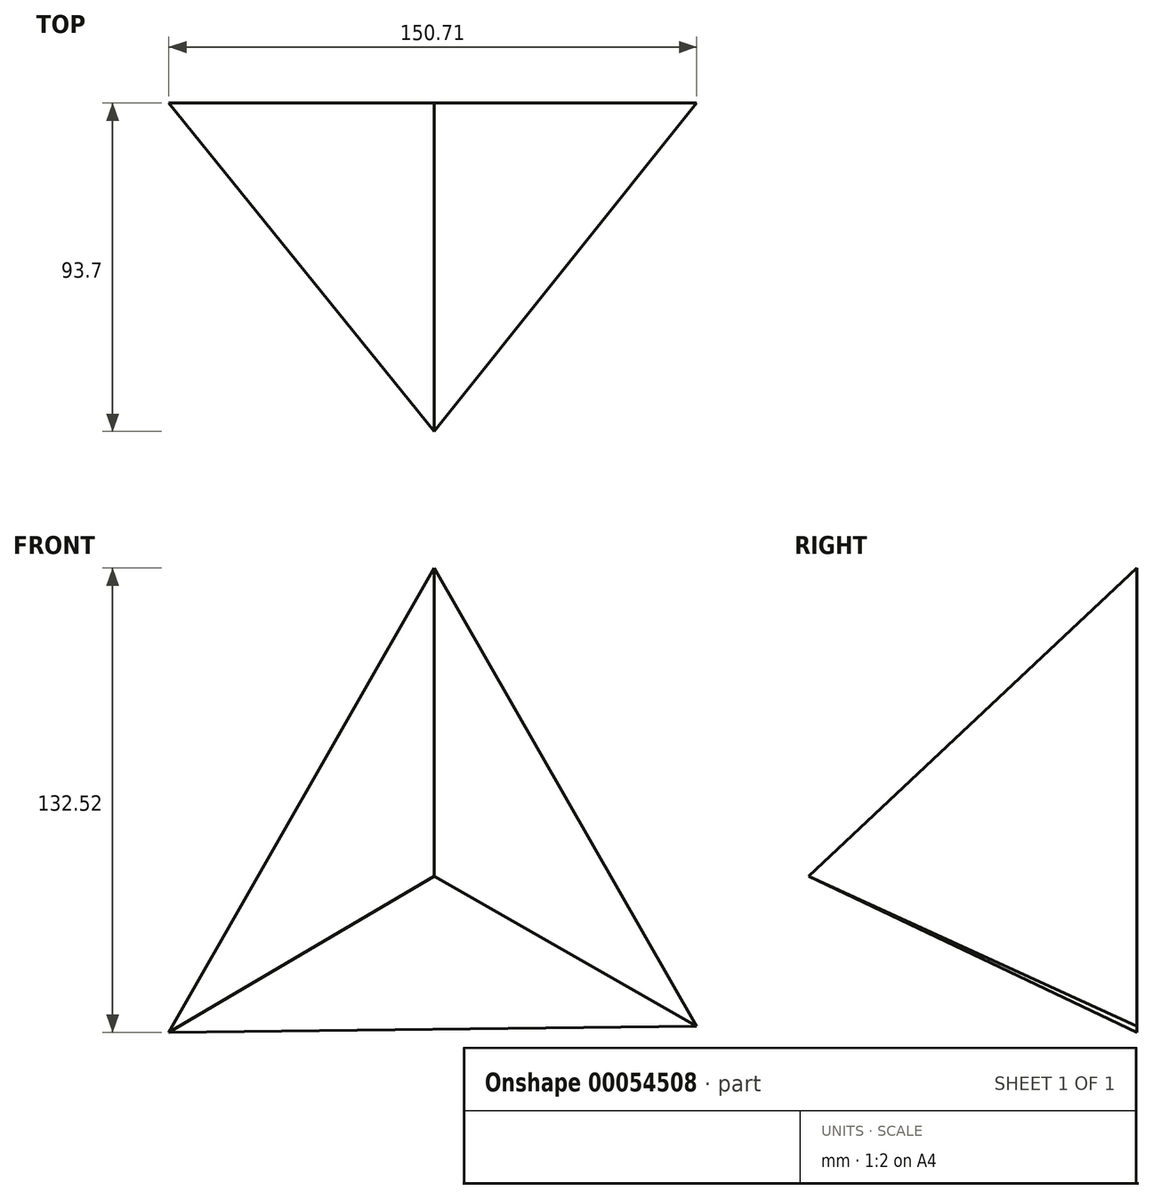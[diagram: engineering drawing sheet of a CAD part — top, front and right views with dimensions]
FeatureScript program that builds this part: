
annotation { "Feature Type Name" : "Feature", "Feature Type Description" : "" }
export const myFeature = defineFeature(function(context is Context, id is Id, definition is map)
    precondition{}
    {
        {
            var Q0;
            Q0=qCreatedBy(makeId("Front.planeOp"),FACE);
            var sketch = newSketch(context, id + "F0", { "sketchPlane" : qUnion([Q0])});
            skLineSegment(sketch, "E0", {"start": v(0, 56.73) * mm, "end": v(-75.79, -75.79) * mm});
            skLineSegment(sketch, "E1", {"start": v(0, 56.73) * mm, "end": v(74.92, -74.05) * mm});
            skLineSegment(sketch, "E2", {"start": v(74.92, -74.05) * mm, "end": v(-75.79, -75.79) * mm});
            skSolve(sketch);
        }
        {
            var Q0;
            Q0=makeQuery(id+"F0.imprint","IMPRINT",FACE,{"disambiguationData":[TD([[makeQuery(id+"F0.imprint","IMPRINT",EDGE,{"derivedFrom":sQuery(id+"F0.wireOp",EDGE,"E0")}),1.0]])]});
            extrude(context, id + "F1", {"entities" : qUnion([Q0]), "depth" : 101.6 * mm, "hasDraft" : true, "draftAngle" : 25 * degree, "draftPullDirection" : true});
        }
    });
